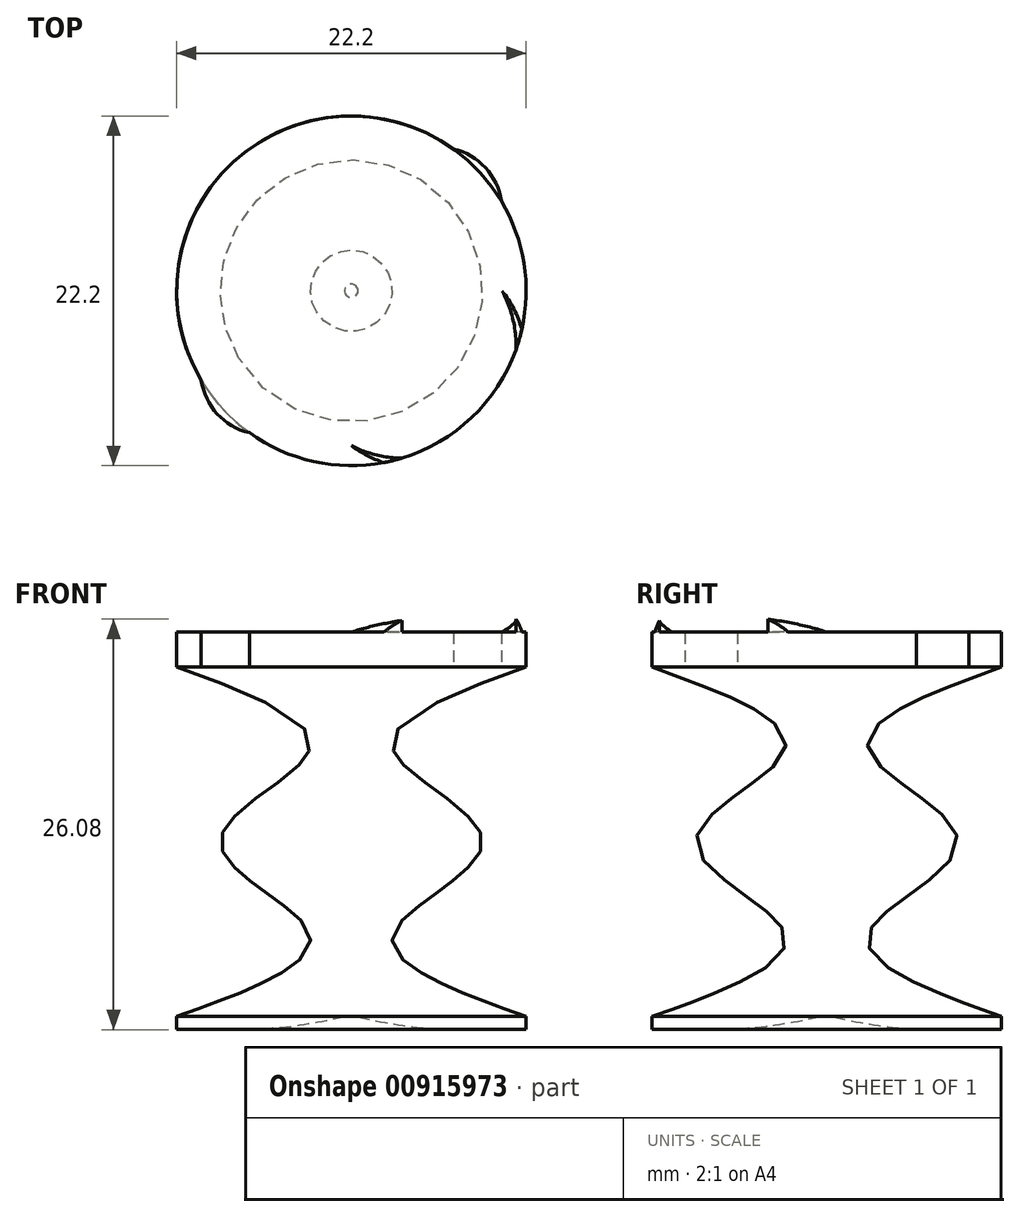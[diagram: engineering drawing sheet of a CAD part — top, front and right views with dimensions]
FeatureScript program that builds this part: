
annotation { "Feature Type Name" : "Feature", "Feature Type Description" : "" }
export const myFeature = defineFeature(function(context is Context, id is Id, definition is map)
    precondition{}
    {
        {
            var Q0;
            Q0=qCreatedBy(makeId("Top.planeOp"),FACE);
            cPlane(context, id + "F0", {"entities" : qUnion([Q0]), "cplaneType" : CPlaneType.OFFSET, "offset" : 12.7 * mm, "width" : 152.4 * mm, "height" : 152.4 * mm});
        }
        {
            var Q0;
            Q0=qCreatedBy(makeId("Top.planeOp"),FACE);
            cPlane(context, id + "F1", {"entities" : qUnion([Q0]), "cplaneType" : CPlaneType.OFFSET, "offset" : 12.7 * mm, "oppositeDirection" : true, "width" : 152.4 * mm, "height" : 152.4 * mm});
        }
        {
            var Q0;
            Q0=qCreatedBy(makeId("Top.planeOp"),FACE);
            cPlane(context, id + "F2", {"entities" : qUnion([Q0]), "cplaneType" : CPlaneType.OFFSET, "offset" : 6.35 * mm, "width" : 152.4 * mm, "height" : 152.4 * mm});
        }
        {
            var Q0;
            Q0=qCreatedBy(makeId("Top.planeOp"),FACE);
            cPlane(context, id + "F3", {"entities" : qUnion([Q0]), "cplaneType" : CPlaneType.OFFSET, "offset" : 6.35 * mm, "oppositeDirection" : true, "width" : 152.4 * mm, "height" : 152.4 * mm});
        }
        {
            var Q0;
            Q0=qCreatedBy(id+"F0.planeOp",FACE);
            var sketch = newSketch(context, id + "F4", { "sketchPlane" : qUnion([Q0])});
            skCircle(sketch, "E0", {"center": v(0, 0) * mm, "radius": 12.7 * mm});
            skSolve(sketch);
        }
        {
            var Q0;
            Q0=qCreatedBy(id+"F1.planeOp",FACE);
            var sketch = newSketch(context, id + "F5", { "sketchPlane" : qUnion([Q0])});
            skCircle(sketch, "E1.0.0", {"center": v(0, 0) * mm, "radius": 12.7 * mm});
            skSolve(sketch);
        }
        {
            var Q0;
            Q0=qCreatedBy(makeId("Top.planeOp"),FACE);
            var sketch = newSketch(context, id + "F6", { "sketchPlane" : qUnion([Q0])});
            skCircle(sketch, "E2", {"center": v(0, 0) * mm, "radius": 9.52 * mm});
            skSolve(sketch);
        }
        {
            var Q0;
            Q0=qCreatedBy(id+"F2.planeOp",FACE);
            var sketch = newSketch(context, id + "F7", { "sketchPlane" : qUnion([Q0])});
            skCircle(sketch, "E3", {"center": v(0, 0) * mm, "radius": 3.18 * mm});
            skSolve(sketch);
        }
        {
            var Q0;
            Q0=qCreatedBy(id+"F3.planeOp",FACE);
            var sketch = newSketch(context, id + "F8", { "sketchPlane" : qUnion([Q0])});
            skCircle(sketch, "E4", {"center": v(0, 0) * mm, "radius": 3.18 * mm});
            skSolve(sketch);
        }
        {
            var Q0;
            Q0=makeQuery(id+"F5.imprint","IMPRINT",FACE,{"disambiguationData":[TD([[makeQuery(id+"F5.imprint","IMPRINT",EDGE,{"derivedFrom":sQuery(id+"F5.wireOp",EDGE,"E1.0.0")}),1.0]])]});
            var Q1;
            Q1=makeQuery(id+"F8.imprint","IMPRINT",FACE,{"disambiguationData":[TD([[makeQuery(id+"F8.imprint","IMPRINT",EDGE,{"derivedFrom":sQuery(id+"F8.wireOp",EDGE,"E4")}),1.0]])]});
            var Q2;
            Q2=makeQuery(id+"F6.imprint","IMPRINT",FACE,{"disambiguationData":[TD([[makeQuery(id+"F6.imprint","IMPRINT",EDGE,{"derivedFrom":sQuery(id+"F6.wireOp",EDGE,"E2")}),1.0]])]});
            var Q3;
            Q3=makeQuery(id+"F7.imprint","IMPRINT",FACE,{"disambiguationData":[TD([[makeQuery(id+"F7.imprint","IMPRINT",EDGE,{"derivedFrom":sQuery(id+"F7.wireOp",EDGE,"E3")}),1.0]])]});
            var Q4;
            Q4=makeQuery(id+"F4.imprint","IMPRINT",FACE,{"disambiguationData":[TD([[makeQuery(id+"F4.imprint","IMPRINT",EDGE,{"derivedFrom":sQuery(id+"F4.wireOp",EDGE,"E0")}),1.0]])]});
            loft(context, id + "F9", {"sheetProfilesArray" : [{ "sheetProfileEntities" : qUnion([Q0]) }, { "sheetProfileEntities" : qUnion([Q1]) }, { "sheetProfileEntities" : qUnion([Q2]) }, { "sheetProfileEntities" : qUnion([Q3]) }, { "sheetProfileEntities" : qUnion([Q4]) }]});
        }
        {
            var Q0;
            Q0=qCreatedBy(makeId("Right.planeOp"),FACE);
            var sketch = newSketch(context, id + "F10", { "sketchPlane" : qUnion([Q0])});
            skLineSegment(sketch, "E5", {"start": v(0, 12.77) * mm, "end": v(0, 16.7) * mm, "construction": true});
            skSolve(sketch);
        }
        {
            var Q0;
            Q0=makeQuery(id+"F4.imprint","IMPRINT",FACE,{"disambiguationData":[TD([[makeQuery(id+"F4.imprint","IMPRINT",EDGE,{"derivedFrom":sQuery(id+"F4.wireOp",EDGE,"E0")}),1.0]])]});
            var sketch = newSketch(context, id + "F11", { "sketchPlane" : qUnion([Q0])});
            skCircle(sketch, "E6.0.0", {"center": v(0, 0) * mm, "radius": 12.7 * mm});
            skSolve(sketch);
        }
        {
            var Q0;
            {var subQ0=sQuery(id+"F11.wireOp",EDGE,"mRxZaYF6-lXSe-QfLY-RrVI-3R1xbwflJLP2");Q0=makeQuery(id+"F11.imprint","IMPRINT",FACE,{"disambiguationData":[TD([[makeQuery(id+"F11.imprint","IMPRINT",EDGE,{"derivedFrom":subQ0}),1.0]])]});}
            var Q1;
            {var subQ0=sQuery(id+"F11.wireOp",EDGE,"mRxZaYF6-lXSe-QfLY-RrVI-3R1xbwflJLP2");var subQ1=sQuery(id+"F11.wireOp",EDGE,"E6.0.0");var subQ2=makeQuery(id+"F11.imprint","INTERSECT",VERTEX,{"disambiguationData":[OD(0.0)],"derivedFrom":[subQ1,subQ0]});Q1=makeQuery(id+"F11.imprint","IMPRINT",FACE,{"disambiguationData":[TD([[makeQuery(id+"F11.imprint","IMPRINT",EDGE,{"disambiguationData":[TD([[subQ2,1.0]])],"derivedFrom":subQ1}),1.0]])]});}
            extrude(context, id + "F12", {"entities" : qUnion([Q0, Q1]), "operationType" : NewBodyOperationType.ADD, "depth" : 2.54 * mm, "offsetDistance" : 25.4 * mm});
        }
        {
            var Q0;
            Q0=makeQuery(id+"F12.opExtrude","CAP_FACE",FACE,{"disambiguationData":[OSD([sQuery(id+"F11.wireOp",EDGE,"E6.0.0")])],"isStart":false});
            var sketch = newSketch(context, id + "F13", { "sketchPlane" : qUnion([Q0])});
            skArc(sketch, "E7", {"start": v(0, -11.25) * mm, "mid": v(10.45, -10.47) * mm, "end": v(10.95, 0) * mm});
            skArc(sketch, "E8", {"start": v(0, -11.25) * mm, "mid": v(9.63, -9.67) * mm, "end": v(10.95, 0) * mm});
            skSolve(sketch);
        }
        {
            var Q0;
            {var subQ0=sQuery(id+"F13.wireOp",EDGE,"E7");var subQ1=makeQuery(id+"F12.opExtrude","CAP_EDGE",EDGE,{"disambiguationData":[OSD([sQuery(id+"F11.wireOp",EDGE,"E6.0.0")])],"isStart":false});var subQ2=makeQuery(id+"F13.imprint","INTERSECT",VERTEX,{"disambiguationData":[OD(0.0)],"derivedFrom":[subQ1,subQ0]});Q0=makeQuery(id+"F13.imprint","IMPRINT",FACE,{"disambiguationData":[TD([[makeQuery(id+"F13.imprint","IMPRINT",EDGE,{"disambiguationData":[TD([[subQ2,-1.0]])],"derivedFrom":subQ0}),1.0]])]});}
            var Q1;
            {var subQ0=sQuery(id+"F13.wireOp",EDGE,"E8");var subQ1=sQuery(id+"F13.wireOp",EDGE,"E7");var subQ2=makeQuery(id+"F13.imprint","INTERSECT",VERTEX,{"disambiguationData":[OD(1.0)],"derivedFrom":[subQ1,subQ0]});Q1=makeQuery(id+"F13.imprint","IMPRINT",FACE,{"disambiguationData":[TD([[makeQuery(id+"F13.imprint","IMPRINT",EDGE,{"disambiguationData":[TD([[subQ2,1.0]])],"derivedFrom":subQ1}),1.0]])]});}
            var Q2;
            {var subQ0=sQuery(id+"F13.wireOp",EDGE,"E8");var subQ1=sQuery(id+"F13.wireOp",EDGE,"E7");var subQ2=makeQuery(id+"F13.imprint","INTERSECT",VERTEX,{"disambiguationData":[OD(0.0)],"derivedFrom":[subQ1,subQ0]});Q2=makeQuery(id+"F13.imprint","IMPRINT",FACE,{"disambiguationData":[TD([[makeQuery(id+"F13.imprint","IMPRINT",EDGE,{"disambiguationData":[TD([[subQ2,-1.0]])],"derivedFrom":subQ1}),1.0]])]});}
            extrude(context, id + "F14", {"entities" : qUnion([Q0, Q1, Q2]), "operationType" : NewBodyOperationType.ADD, "depth" : 2.54 * mm, "offsetDistance" : 25.4 * mm});
        }
        {
            var Q0;
            Q0=makeQuery(id+"FsqxvaSzaSi3oDm_1.-1.F14.opExtrude","CAP_EDGE",EDGE,{"disambiguationData":[OSD([sQuery(id+"F13.wireOp",EDGE,"E7")])],"isStart":false});
            var Q1;
            Q1=makeQuery(id+"FsqxvaSzaSi3oDm_1.-2.F14.opExtrude","CAP_EDGE",EDGE,{"disambiguationData":[OSD([sQuery(id+"F13.wireOp",EDGE,"E7")])],"isStart":false});
            var Q2;
            Q2=makeQuery(id+"FsqxvaSzaSi3oDm_1.-3.F14.opExtrude","CAP_EDGE",EDGE,{"disambiguationData":[OSD([sQuery(id+"F13.wireOp",EDGE,"E7")])],"isStart":false});
            var Q3;
            Q3=makeQuery(id+"F14.opExtrude","CAP_EDGE",EDGE,{"disambiguationData":[OSD([sQuery(id+"F13.wireOp",EDGE,"E7")])],"isStart":false});
            fillet(context, id + "F15", {"entities" : qUnion([Q0, Q1, Q2, Q3]), "radius" : 5.08 * mm, "tangentPropagation" : true, "allowEdgeOverflow" : false});
        }
        {
            var Q0;
            Q0=qCreatedBy(id+"F0.planeOp",FACE);
            var sketch = newSketch(context, id + "F16", { "sketchPlane" : qUnion([Q0])});
            skArc(sketch, "E9", {"start": v(-10.77, -4.53) * mm, "mid": v(-9.73, -8.96) * mm, "end": v(-5.39, -10.34) * mm});
            skArc(sketch, "E10.MirrorCS", {"start": v(-10.77, 4.53) * mm, "mid": v(-9.73, 8.96) * mm, "end": v(-5.39, 10.34) * mm});
            skArc(sketch, "E11.MirrorCS", {"start": v(10.77, -4.53) * mm, "mid": v(9.73, -8.96) * mm, "end": v(5.39, -10.34) * mm});
            skArc(sketch, "E12.MirrorCS", {"start": v(10.77, 4.53) * mm, "mid": v(9.73, 8.96) * mm, "end": v(5.39, 10.34) * mm});
            skLineSegment(sketch, "E13", {"start": v(5.39, 10.34) * mm, "end": v(10.77, 4.53) * mm});
            skLineSegment(sketch, "E14", {"start": v(10.77, -4.53) * mm, "end": v(5.39, -10.34) * mm});
            skLineSegment(sketch, "E15", {"start": v(-5.39, 10.34) * mm, "end": v(-10.77, 4.53) * mm});
            skLineSegment(sketch, "E16", {"start": v(-10.77, -4.53) * mm, "end": v(-5.39, -10.34) * mm});
            skSolve(sketch);
        }
        {
            var Q0;
            Q0=makeQuery(id+"F16.imprint","IMPRINT",FACE,{"disambiguationData":[TD([[makeQuery(id+"F16.imprint","IMPRINT",EDGE,{"derivedFrom":sQuery(id+"F16.wireOp",EDGE,"E12.MirrorCS")}),1.0]])]});
            var Q1;
            Q1=makeQuery(id+"F16.imprint","IMPRINT",FACE,{"disambiguationData":[TD([[makeQuery(id+"F16.imprint","IMPRINT",EDGE,{"derivedFrom":sQuery(id+"F16.wireOp",EDGE,"E11.MirrorCS")}),-1.0]])]});
            var Q2;
            Q2=makeQuery(id+"F16.imprint","IMPRINT",FACE,{"disambiguationData":[TD([[makeQuery(id+"F16.imprint","IMPRINT",EDGE,{"derivedFrom":sQuery(id+"F16.wireOp",EDGE,"E9")}),1.0]])]});
            var Q3;
            Q3=makeQuery(id+"F16.imprint","IMPRINT",FACE,{"disambiguationData":[TD([[makeQuery(id+"F16.imprint","IMPRINT",EDGE,{"derivedFrom":sQuery(id+"F16.wireOp",EDGE,"E10.MirrorCS")}),-1.0]])]});
            extrude(context, id + "F17", {"entities" : qUnion([Q0, Q1, Q2, Q3]), "operationType" : NewBodyOperationType.ADD, "depth" : 2.54 * mm, "offsetDistance" : 25.4 * mm});
        }
        {
            var Q0;
            Q0=makeQuery(id+"F9.opLoft","SWEPT_BODY",BODY,{"disambiguationData":[OSD([makeQuery(id+"F4.imprint","IMPRINT",FACE,{"disambiguationData":[TD([[makeQuery(id+"F4.imprint","IMPRINT",EDGE,{"derivedFrom":sQuery(id+"F4.wireOp",EDGE,"E0")}),1.0]])]}),makeQuery(id+"F5.imprint","IMPRINT",FACE,{"disambiguationData":[TD([[makeQuery(id+"F5.imprint","IMPRINT",EDGE,{"derivedFrom":sQuery(id+"F5.wireOp",EDGE,"E1.0.0")}),1.0]])]}),sQuery(id+"F6.wireOp",EDGE,"E2"),sQuery(id+"F7.wireOp",EDGE,"E3"),sQuery(id+"F8.wireOp",EDGE,"E4")])]});
            var Q1;
            Q1=qCreatedBy(makeId("Origin.pointOp"),VERTEX);
            transform(context, id + "F18", {"entities" : qUnion([Q0]), "transformType" : TransformType.SCALE_UNIFORMLY, "scale" : 0.95, "scalePoint" : qUnion([Q1]), "makeCopy" : false});
        }
        {
            var Q0;
            Q0=qCreatedBy(makeId("Front.planeOp"),FACE);
            var sketch = newSketch(context, id + "F19", { "sketchPlane" : qUnion([Q0])});
            skLineSegment(sketch, "E17", {"start": v(-12.06, -12.06) * mm, "end": v(-12.06, -12.96) * mm});
            skLineSegment(sketch, "E18", {"start": v(-12.06, -12.96) * mm, "end": v(-7.68, -12.96) * mm});
            skArc(sketch, "E19", {"start": v(-7.68, -12.96) * mm, "mid": v(-4.04, -12.74) * mm, "end": v(-0.46, -12.07) * mm});
            skLineSegment(sketch, "E20", {"start": v(-0.46, -12.07) * mm, "end": v(0, -12.07) * mm});
            skLineSegment(sketch, "E21", {"start": v(-0.46, -12.07) * mm, "end": v(-12.06, -12.06) * mm});
            skPoint(sketch, "E22", {"position": v(0, -12.07) * mm});
            skSolve(sketch);
        }
        {
            var Q0;
            Q0=qCreatedBy(makeId("Front.planeOp"),FACE);
            var sketch = newSketch(context, id + "F20", { "sketchPlane" : qUnion([Q0])});
            skLineSegment(sketch, "E23", {"start": v(0, -11.38) * mm, "end": v(0, -13.01) * mm, "construction": true});
            skSolve(sketch);
        }
        {
            var Q0;
            Q0=makeQuery(id+"F19.imprint","IMPRINT",FACE,{"disambiguationData":[TD([[makeQuery(id+"F19.imprint","IMPRINT",EDGE,{"derivedFrom":sQuery(id+"F19.wireOp",EDGE,"E17")}),1.0]])]});
            var Q1;
            Q1=sQuery(id+"F20.wireOp",EDGE,"E23");
            revolve(context, id + "F21", {"operationType" : NewBodyOperationType.ADD, "surfaceOperationType" : NewSurfaceOperationType.NEW, "entities" : qUnion([Q0]), "axis" : qUnion([Q1]), "revolveType" : RevolveType.FULL});
        }
        {
            var Q0;
            Q0=makeQuery(id+"F9.opLoft","SWEPT_BODY",BODY,{"disambiguationData":[OSD([makeQuery(id+"F4.imprint","IMPRINT",FACE,{"disambiguationData":[TD([[makeQuery(id+"F4.imprint","IMPRINT",EDGE,{"derivedFrom":sQuery(id+"F4.wireOp",EDGE,"E0")}),1.0]])]}),makeQuery(id+"F5.imprint","IMPRINT",FACE,{"disambiguationData":[TD([[makeQuery(id+"F5.imprint","IMPRINT",EDGE,{"derivedFrom":sQuery(id+"F5.wireOp",EDGE,"E1.0.0")}),1.0]])]}),sQuery(id+"F6.wireOp",EDGE,"E2"),sQuery(id+"F7.wireOp",EDGE,"E3"),sQuery(id+"F8.wireOp",EDGE,"E4")])]});
            var Q1;
            Q1=qCreatedBy(makeId("Origin.pointOp"),VERTEX);
            transform(context, id + "F22", {"entities" : qUnion([Q0]), "transformType" : TransformType.SCALE_UNIFORMLY, "scale" : 0.92, "scalePoint" : qUnion([Q1]), "makeCopy" : false});
        }
    });
